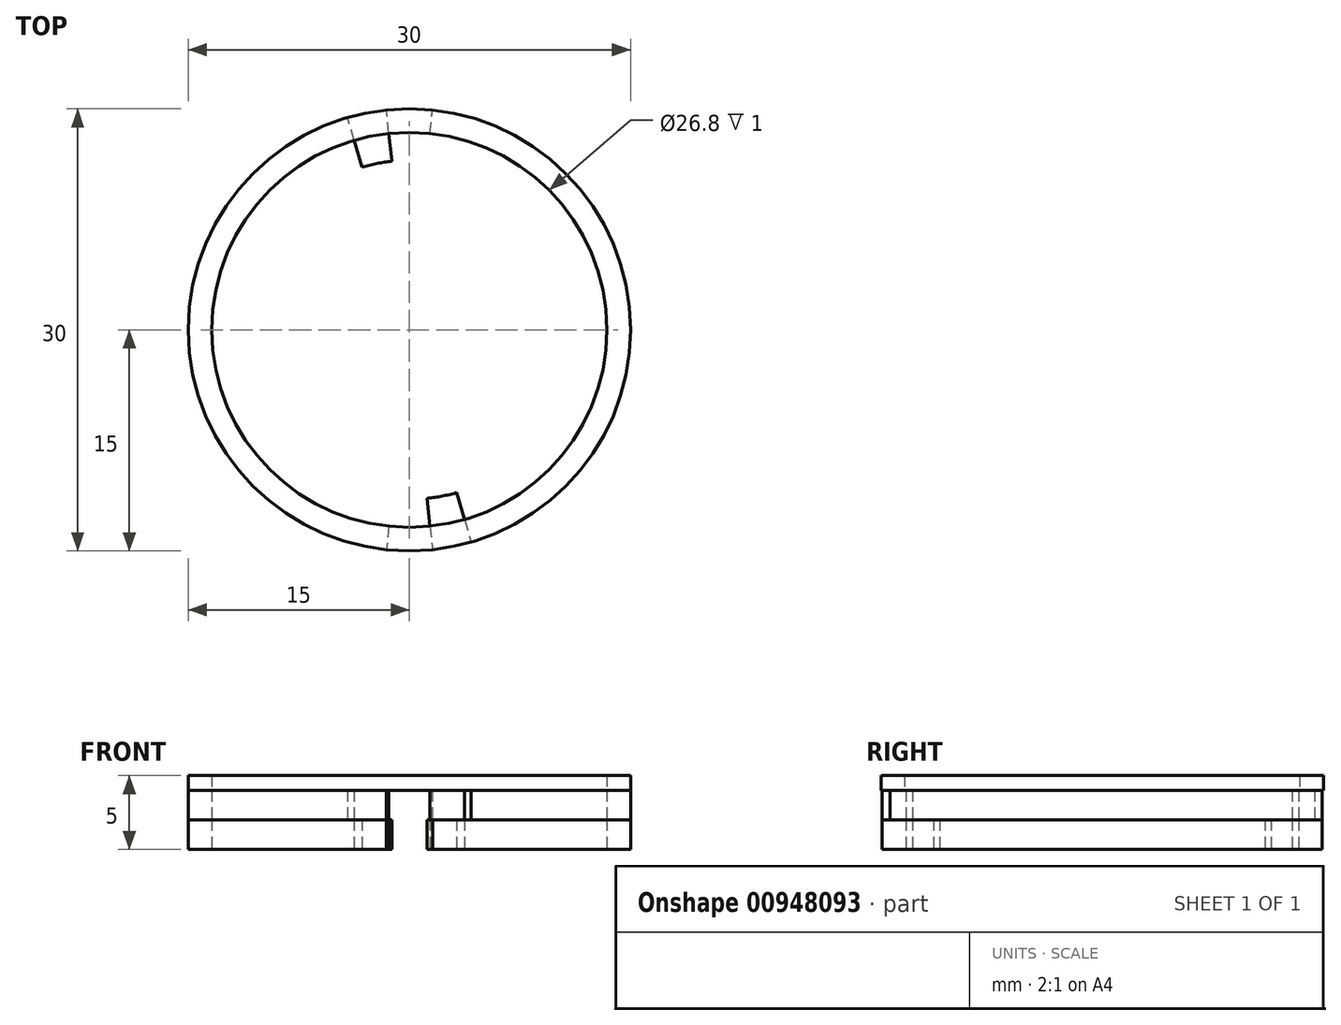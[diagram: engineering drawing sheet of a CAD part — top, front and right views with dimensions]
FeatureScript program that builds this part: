
annotation { "Feature Type Name" : "Feature", "Feature Type Description" : "" }
export const myFeature = defineFeature(function(context is Context, id is Id, definition is map)
    precondition{}
    {
        {
            var Q0;
            Q0=qCreatedBy(makeId("Top.planeOp"),FACE);
            var sketch = newSketch(context, id + "F0", { "sketchPlane" : qUnion([Q0])});
            skCircle(sketch, "E0", {"center": v(0, 0) * mm, "radius": 15 * mm});
            skCircle(sketch, "E1", {"center": v(0, 0) * mm, "radius": 13.4 * mm});
            skCircle(sketch, "E2", {"center": v(0, 0) * mm, "radius": 11.5 * mm});
            skLineSegment(sketch, "E3", {"start": v(0, 0) * mm, "end": v(-1.4, 13.33) * mm});
            skLineSegment(sketch, "E4", {"start": v(0, 0) * mm, "end": v(-3.74, 12.87) * mm});
            skLineSegment(sketch, "E5", {"start": v(-1.4, 13.33) * mm, "end": v(1.4, 13.33) * mm});
            skLineSegment(sketch, "E6", {"start": v(-1.4, 13.33) * mm, "end": v(-1.56, 14.92) * mm});
            skLineSegment(sketch, "E7", {"start": v(1.4, 13.33) * mm, "end": v(1.57, 14.92) * mm});
            skLineSegment(sketch, "E8.MirrorCS", {"start": v(-1.4, -13.33) * mm, "end": v(-1.56, -14.92) * mm});
            skLineSegment(sketch, "E9.MirrorCS", {"start": v(-1.4, -13.33) * mm, "end": v(1.4, -13.33) * mm});
            skLineSegment(sketch, "E10.MirrorCS", {"start": v(1.4, -13.33) * mm, "end": v(1.57, -14.92) * mm});
            skLineSegment(sketch, "E11", {"start": v(0, 0) * mm, "end": v(1.4, -13.33) * mm});
            skLineSegment(sketch, "E12", {"start": v(0, 0) * mm, "end": v(3.74, -12.87) * mm});
            skSolve(sketch);
        }
        {
            var Q0;
            {var subQ3=sQuery(id+"F0.wireOp",EDGE,"E4");var subQ5=sQuery(id+"F0.wireOp",EDGE,"E2");var subQ6=makeQuery(id+"F0.imprint","INTERSECT",VERTEX,{"derivedFrom":[subQ5,subQ3]});Q0=makeQuery(id+"F0.imprint","IMPRINT",FACE,{"disambiguationData":[TD([[makeQuery(id+"F0.imprint","IMPRINT",EDGE,{"disambiguationData":[TD([[subQ6,1.0]])],"derivedFrom":subQ5}),-1.0]])]});}
            var Q1;
            {var subQ0=sQuery(id+"F0.wireOp",EDGE,"E6");Q1=makeQuery(id+"F0.imprint","IMPRINT",FACE,{"disambiguationData":[TD([[makeQuery(id+"F0.imprint","IMPRINT",EDGE,{"derivedFrom":subQ0}),1.0]])]});}
            var Q2;
            {var subQ0=sQuery(id+"F0.wireOp",EDGE,"E7");Q2=makeQuery(id+"F0.imprint","IMPRINT",FACE,{"disambiguationData":[TD([[makeQuery(id+"F0.imprint","IMPRINT",EDGE,{"derivedFrom":subQ0}),-1.0]])]});}
            var Q3;
            {var subQ0=sQuery(id+"F0.wireOp",EDGE,"E11");var subQ5=sQuery(id+"F0.wireOp",EDGE,"E2");var subQ6=makeQuery(id+"F0.imprint","INTERSECT",VERTEX,{"derivedFrom":[subQ5,subQ0]});Q3=makeQuery(id+"F0.imprint","IMPRINT",FACE,{"disambiguationData":[TD([[makeQuery(id+"F0.imprint","IMPRINT",EDGE,{"disambiguationData":[TD([[subQ6,-1.0]])],"derivedFrom":subQ5}),-1.0]])]});}
            extrude(context, id + "F1", {"entities" : qUnion([Q0, Q1, Q2, Q3]), "depth" : 2 * mm, "offsetDistance" : 25 * mm});
        }
        {
            var Q0;
            Q0=makeQuery(id+"F1.opExtrude","CAP_FACE",FACE,{"disambiguationData":[OSD([sQuery(id+"F0.wireOp",EDGE,"E0"),sQuery(id+"F0.wireOp",EDGE,"E1"),sQuery(id+"F0.wireOp",EDGE,"E2"),sQuery(id+"F0.wireOp",EDGE,"E3"),sQuery(id+"F0.wireOp",EDGE,"E4"),sQuery(id+"F0.wireOp",EDGE,"E6"),sQuery(id+"F0.wireOp",EDGE,"E8.MirrorCS")])],"isStart":false});
            var sketch = newSketch(context, id + "F2", { "sketchPlane" : qUnion([Q0])});
            skCircle(sketch, "E13", {"center": v(0, 0) * mm, "radius": 15 * mm});
            skLineSegment(sketch, "E14", {"start": v(0, 0) * mm, "end": v(-4.19, 14.4) * mm});
            skLineSegment(sketch, "E15", {"start": v(0, 0) * mm, "end": v(4.19, -14.4) * mm});
            skLineSegment(sketch, "E16", {"start": v(-1.56, -14.92) * mm, "end": v(0, 0) * mm});
            skLineSegment(sketch, "E17", {"start": v(0, 0) * mm, "end": v(1.56, 14.92) * mm});
            skCircle(sketch, "E18", {"center": v(0, 0) * mm, "radius": 13.4 * mm});
            skSolve(sketch);
        }
        {
            var Q0;
            {var subQ0=sQuery(id+"F2.wireOp",EDGE,"E15");var subQ1=sQuery(id+"F2.wireOp",EDGE,"E13");var subQ2=makeQuery(id+"F2.imprint","INTERSECT",VERTEX,{"derivedFrom":[subQ1,subQ0]});Q0=makeQuery(id+"F2.imprint","IMPRINT",FACE,{"disambiguationData":[TD([[makeQuery(id+"F2.imprint","IMPRINT",EDGE,{"disambiguationData":[TD([[subQ2,-1.0]])],"derivedFrom":subQ1}),1.0]])]});}
            var Q1;
            {var subQ0=sQuery(id+"F2.wireOp",EDGE,"E16");var subQ1=sQuery(id+"F2.wireOp",EDGE,"E13");var subQ2=makeQuery(id+"F2.imprint","INTERSECT",VERTEX,{"derivedFrom":[subQ1,subQ0]});Q1=makeQuery(id+"F2.imprint","IMPRINT",FACE,{"disambiguationData":[TD([[makeQuery(id+"F2.imprint","IMPRINT",EDGE,{"disambiguationData":[TD([[subQ2,1.0]])],"derivedFrom":subQ1}),1.0]])]});}
            extrude(context, id + "F3", {"entities" : qUnion([Q0, Q1]), "depth" : 2 * mm, "offsetDistance" : 25 * mm});
        }
        {
            var Q0;
            Q0=makeQuery(id+"F3.opExtrude","CAP_FACE",FACE,{"disambiguationData":[OSD([sQuery(id+"F2.wireOp",EDGE,"E13"),sQuery(id+"F2.wireOp",EDGE,"E14"),sQuery(id+"F2.wireOp",EDGE,"E16"),sQuery(id+"F2.wireOp",EDGE,"E18")])],"isStart":false});
            var sketch = newSketch(context, id + "F4", { "sketchPlane" : qUnion([Q0])});
            skCircle(sketch, "E19", {"center": v(0, 0) * mm, "radius": 15 * mm});
            skCircle(sketch, "E20", {"center": v(0, 0) * mm, "radius": 13.4 * mm});
            skSolve(sketch);
        }
        {
            var Q0;
            {var subQ2=makeQuery(id+"F3.opExtrude","CAP_EDGE",EDGE,{"disambiguationData":[OSD([sQuery(id+"F2.wireOp",EDGE,"E14")])],"isStart":false});Q0=makeQuery(id+"F4.imprint","IMPRINT",FACE,{"disambiguationData":[TD([[makeQuery(id+"F4.imprint","IMPRINT",EDGE,{"derivedFrom":subQ2}),1.0]])]});}
            var Q1;
            {var subQ2=makeQuery(id+"F3.opExtrude","CAP_EDGE",EDGE,{"disambiguationData":[OSD([sQuery(id+"F2.wireOp",EDGE,"E14")])],"isStart":false});Q1=makeQuery(id+"F4.imprint","IMPRINT",FACE,{"disambiguationData":[TD([[makeQuery(id+"F4.imprint","IMPRINT",EDGE,{"derivedFrom":subQ2}),-1.0]])]});}
            extrude(context, id + "F5", {"entities" : qUnion([Q0, Q1]), "depth" : 1 * mm, "offsetDistance" : 25 * mm});
        }
    });
